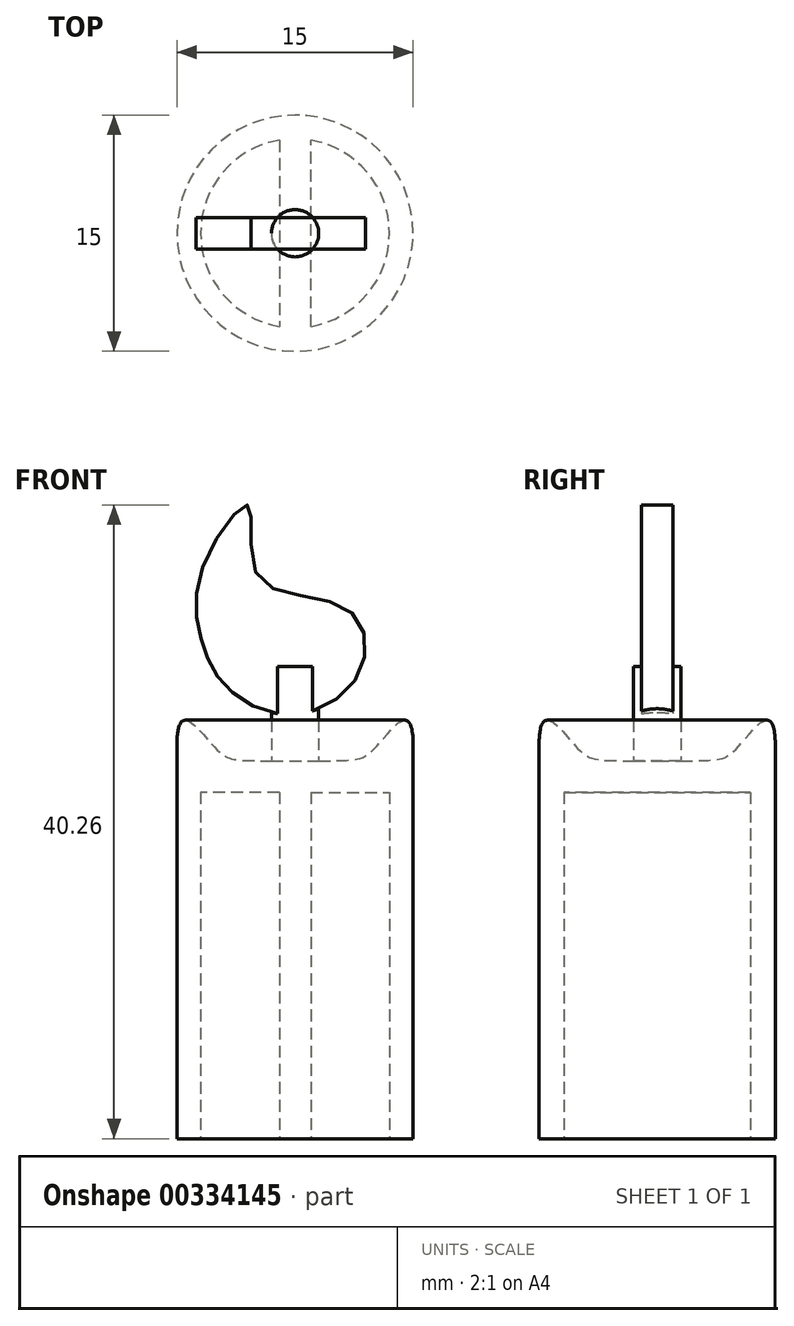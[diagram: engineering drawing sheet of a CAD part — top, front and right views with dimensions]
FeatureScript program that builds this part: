
annotation { "Feature Type Name" : "Feature", "Feature Type Description" : "" }
export const myFeature = defineFeature(function(context is Context, id is Id, definition is map)
    precondition{}
    {
        {
            var Q0;
            Q0=qCreatedBy(makeId("Front.planeOp"),FACE);
            var sketch = newSketch(context, id + "F0", { "sketchPlane" : qUnion([Q0])});
            skLineSegment(sketch, "E0.bottom", {"start": v(0, 0) * mm, "end": v(7.5, 0) * mm});
            skLineSegment(sketch, "E0.left", {"start": v(0, 0) * mm, "end": v(0, 25) * mm});
            skLineSegment(sketch, "E0.right", {"start": v(7.5, 0) * mm, "end": v(7.5, 25) * mm});
            skLineSegment(sketch, "E1.top", {"start": v(0, 30) * mm, "end": v(1.5, 30) * mm});
            skLineSegment(sketch, "E1.left", {"start": v(0, 25) * mm, "end": v(0, 30) * mm});
            skLineSegment(sketch, "E1.right", {"start": v(1.5, 24) * mm, "end": v(1.5, 30) * mm});
            skLineSegment(sketch, "E2", {"start": v(0, 25) * mm, "end": v(-7.5, 25) * mm, "construction": true});
            skLineSegment(sketch, "E3", {"start": v(0, 25) * mm, "end": v(7.5, 25) * mm, "construction": true});
            skFitSpline(sketch, "E4", {"points": [v(7.5, 25) * mm, v(5.61, 25.43) * mm, v(4.32, 24.23) * mm, v(1.5, 24) * mm], "startDerivative": vector(0, 25.92) * mm, "endDerivative": vector(-15.3, 0) * mm});
            skLineSegment(sketch, "E5", {"start": v(1.5, 24) * mm, "end": v(0, 24) * mm, "construction": true});
            skSolve(sketch);
        }
        {
            var Q0;
            Q0 = qSketchRegion(id + "F0", true);
            var Q1;
            Q1=sQuery(id+"F0.wireOp",EDGE,"E0.left");
            revolve(context, id + "F1", {"entities" : qUnion([Q0]), "axis" : qUnion([Q1]), "revolveType" : RevolveType.FULL});
        }
        {
            var Q0;
            Q0=qCreatedBy(makeId("Front.planeOp"),FACE);
            var sketch = newSketch(context, id + "F2", { "sketchPlane" : qUnion([Q0])});
            skFitSpline(sketch, "E6", {"points": [v(0, 26.95) * mm, v(4.2, 29.85) * mm, v(3.18, 33.74) * mm, v(-2.37, 35.72) * mm, v(-2.95, 40.22) * mm, v(-5.8, 36.48) * mm, v(-6, 31.85) * mm, v(-4.4, 28.73) * mm, v(0, 26.95) * mm]});
            skSolve(sketch);
        }
        {
            var Q0;
            Q0 = qSketchRegion(id + "F2", true);
            extrude(context, id + "F3", {"entities" : qUnion([Q0]), "operationType" : NewBodyOperationType.ADD, "endBound" : BoundingType.SYMMETRIC, "depth" : 2 * mm});
        }
        {
            var Q0;
            Q0=makeQuery(id+"F1.opRevolve","SWEPT_FACE",FACE,{"disambiguationData":[OSD([sQuery(id+"F0.wireOp",EDGE,"E0.bottom")])]});
            var sketch = newSketch(context, id + "F4", { "sketchPlane" : qUnion([Q0])});
            skArc(sketch, "E7", {"start": v(-1, 5.92) * mm, "mid": v(-6, 0) * mm, "end": v(-1, -5.92) * mm});
            skLineSegment(sketch, "E8", {"start": v(1, 5.92) * mm, "end": v(1, -5.92) * mm});
            skLineSegment(sketch, "E9", {"start": v(1, -5.92) * mm, "end": v(-1, -5.92) * mm, "construction": true});
            skLineSegment(sketch, "E10", {"start": v(-1, -5.92) * mm, "end": v(-1, 5.92) * mm});
            skArc(sketch, "E11.trimOffspring", {"start": v(1, -5.92) * mm, "mid": v(6, 0) * mm, "end": v(1, 5.92) * mm});
            skSolve(sketch);
        }
        {
            var Q0;
            Q0 = qSketchRegion(id + "F4", true);
            extrude(context, id + "F5", {"entities" : qUnion([Q0]), "operationType" : NewBodyOperationType.REMOVE, "oppositeDirection" : true, "depth" : 22 * mm});
        }
    });
